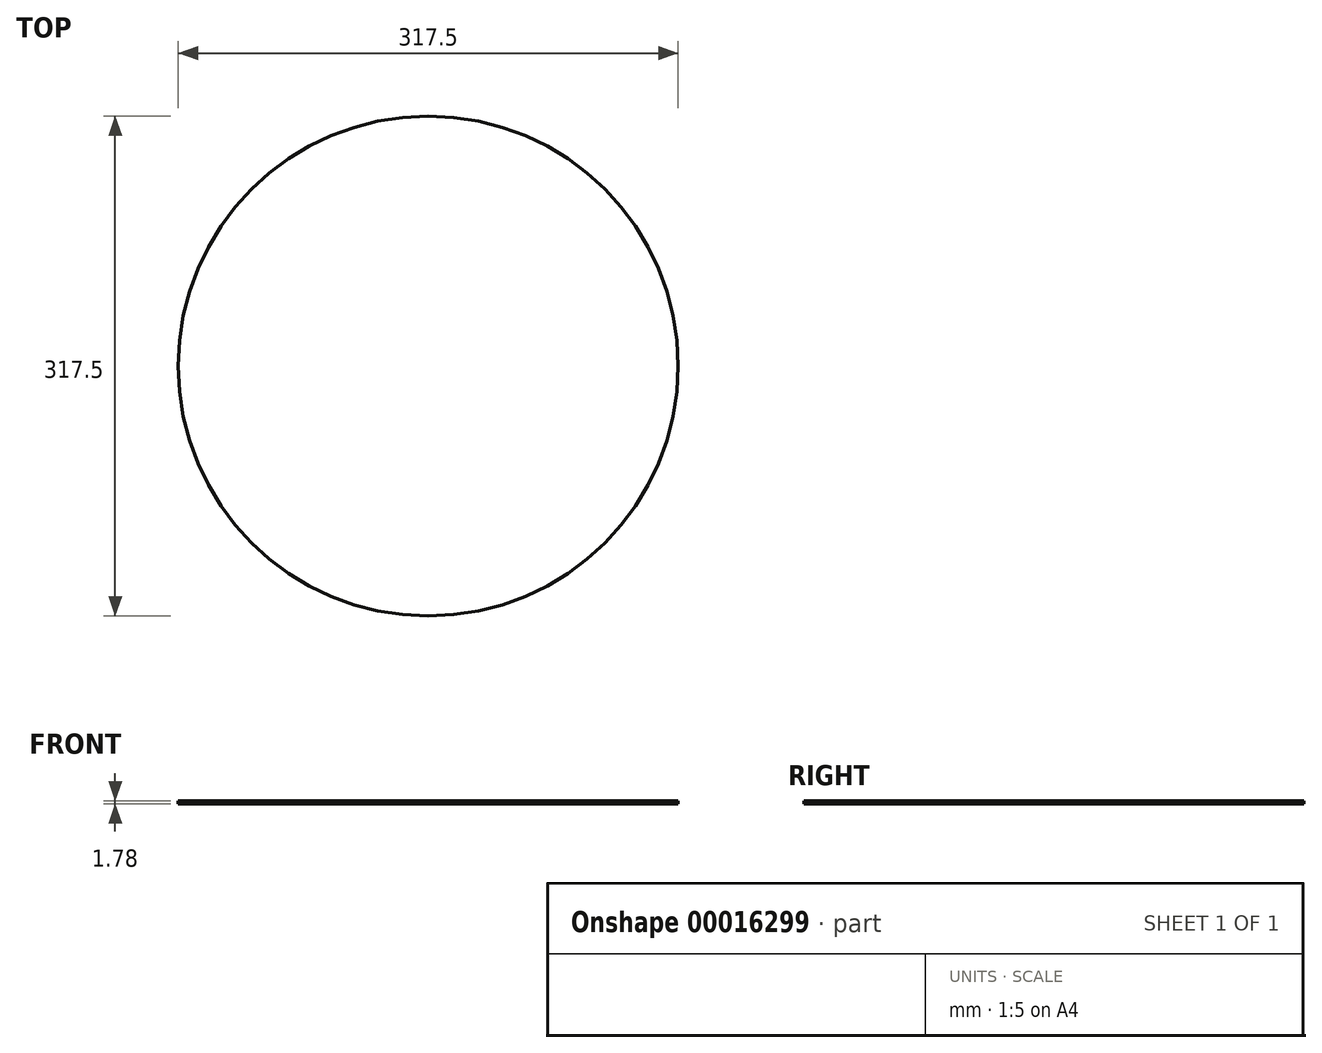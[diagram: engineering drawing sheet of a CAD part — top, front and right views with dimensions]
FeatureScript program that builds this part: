
annotation { "Feature Type Name" : "Feature", "Feature Type Description" : "" }
export const myFeature = defineFeature(function(context is Context, id is Id, definition is map)
    precondition{}
    {
        {
            var Q0;
            Q0=qCreatedBy(makeId("Top.planeOp"),FACE);
            var sketch = newSketch(context, id + "F0", { "sketchPlane" : qUnion([Q0])});
            skCircle(sketch, "E0", {"center": v(0, 0) * mm, "radius": 158.75 * mm});
            skSolve(sketch);
        }
        {
            var Q0;
            Q0 = qSketchRegion(id + "F0", true);
            extrude(context, id + "F1", {"entities" : qUnion([Q0]), "depth" : 1.78 * mm});
        }
    });
